# Revit family: SkylightScreen_KeeSafety_StandingSeamStyle
name_source: partatom
category: Generic Models
units: mm (PartAtom-declared; Revit-internal decimal feet)

## family parameters
Always vertical = Yes
Can host rebar = No
Classification Number = 23.30.80.11
Cut with Voids When Loaded = No
Maintain Annotation Orientation = No
Part Type = Normal
Room Calculation Point = No
Round Connector Dimension = Use Diameter
Shared = No
Work Plane-Based = Yes

## types (1)
- SkylightScreen_KeeSafety_StandingSeamStyle
    Assembly Code = B3020230
    Construction Details = http://www.arcat.com
    Default Elevation = 0' - 0"
    Description = Skylight Screen - Standing Seam Style
    Green Building-LEED = http://www.arcat.com
    Installation Phase = Skylight Screen
    Keynote = 05 52 00
    Maintenance Schedule (Months) = 12
    Manufacturer = Kee Safety, Inc.
    Manufacturer Fax = 716-896-5696
    Manufacturer Website = keesafety.com
    Material = Kee-Safety_Skylight-Screen
    Model = Standing Seam Style
    Product Data = http://www.arcat.com
    Product Properties = http://www.arcat.com
    Revision = R1_11-2012
    Sales Information = http://www.keesafety.com
    Send Message = http://www.arcat.com
    Specification = http://www.arcat.com
    URL = keesafety.com

## geometry (parser evidence)
native form markers: Blend x6, Sweep x2
no freeform markers — native parametric forms only
